# Revit family: КП РАШВОРК  арт.777 .rfa
name_source: partatom
category: Арматура трубопроводов
units: mm (PartAtom-declared; Revit-internal decimal feet)

## family parameters
Всегда вертикально = Нет
На основе рабочей плоскости = Нет
Общий = Нет
При загрузке вырезать с полостями = Да
Размер круглого соединителя = Использовать диаметр
Тип детали = Нормальный

## types (11) — shared parameters
ADSK_Единица измерения = шт
ADSK_Завод-изготовитель = ООО "ТД "РАШВОРК"
URL = https://rwru.ru
Изготовитель = ООО "ТД "РАШВОРК"
Корпус = Латунь CW617N
zero-valued in all types: Отметка по умолчанию

## per-type parameters (varying)
| type | ADSK_Код изделия | ADSK_Масса | ADSK_Наименование | L | Соединитель | Уго_длинна |
| Кран пробковый для манометра РАШВОРК 777-015-25, DN015, PN25, корпус - латунь (CW617N), конус - латунь (CW617N), уплотнение - Viton, ВР/ВР, BSPP, рукоятка-рычаг | 777-015-25 | 0.195 | Кран пробковый для манометра РАШВОРК 777-015-25, DN015, PN25, корпус - латунь (CW617N), конус - латунь (CW617N), уплотнение - Viton, ВР/ВР, BSPP, рукоятка-рычаг | 60 мм | 15 мм | 60 мм |
| Кран шаровой полнопроходной РАШВОРК 707-040-16, DN040, PN16, корпус - GJL-250 (GG25), шар - AISI304, уплотнение шара - PTFE, Ф/Ф | 707-040-16 | 7.5 | Кран шаровой полнопроходной РАШВОРК 707-040-16, DN040, PN16, корпус - GJL-250 (GG25), шар - AISI304, уплотнение шара - PTFE, Ф/Ф | 140 мм | 40 мм | 140 мм |
| Кран шаровой полнопроходной РАШВОРК 707-020-16, DN020, PN16, корпус - GJL-250 (GG25), шар - AISI304, уплотнение шара - PTFE, Ф/ | 707-020-16 | 2 | Кран шаровой полнопроходной РАШВОРК 707-020-16, DN020, PN16, корпус - GJL-250 (GG25), шар - AISI304, уплотнение шара - PTFE, Ф/Ф | 120 мм | 20 мм | 120 мм |
| Кран шаровой полнопроходной РАШВОРК 707-025-16, DN025, PN16, корпус - GJL-250 (GG25), шар - AISI304, уплотнение шара - PTFE, Ф/Ф | 707-025-16 | 2.1 | Кран шаровой полнопроходной РАШВОРК 707-025-16, DN025, PN16, корпус - GJL-250 (GG25), шар - AISI304, уплотнение шара - PTFE, Ф/Ф | 125 мм | 25 мм | 125 мм |
| Кран шаровой полнопроходной РАШВОРК 707-032-16, DN032, PN16, корпус - GJL-250 (GG25), шар - AISI304, уплотнение шара - PTFE, Ф/Ф | 707-032-16 | 5.9 | Кран шаровой полнопроходной РАШВОРК 707-032-16, DN032, PN16, корпус - GJL-250 (GG25), шар - AISI304, уплотнение шара - PTFE, Ф/Ф | 130 мм | 32 мм | 130 мм |
| Кран шаровой полнопроходной РАШВОРК 707-050-16, DN050, PN16, корпус - GJL-250 (GG25), шар - AISI304, уплотнение шара - PTFE, Ф/Ф | 707-050-16 | 8.5 | Кран шаровой полнопроходной РАШВОРК 707-050-16, DN050, PN16, корпус - GJL-250 (GG25), шар - AISI304, уплотнение шара - PTFE, Ф/Ф | 150 мм | 50 мм | 150 мм |
| Кран шаровой полнопроходной РАШВОРК 707-065-16, DN065, PN16, корпус - GJL-250 (GG25), шар - AISI304, уплотнение шара - PTFE, Ф/Ф | 707-065-16 | 13 | Кран шаровой полнопроходной РАШВОРК 707-065-16, DN065, PN16, корпус - GJL-250 (GG25), шар - AISI304, уплотнение шара - PTFE, Ф/Ф | 170 мм | 65 мм | 170 мм |
| Кран шаровой полнопроходной РАШВОРК 707-080-16, DN080, PN16, корпус - GJL-250 (GG25), шар - AISI304, уплотнение шара - PTFE, Ф/Ф | 707-080-16 | 20.5 | Кран шаровой полнопроходной РАШВОРК 707-080-16, DN080, PN16, корпус - GJL-250 (GG25), шар - AISI304, уплотнение шара - PTFE, Ф/Ф | 180 мм | 80 мм | 180 мм |
| Кран шаровой полнопроходной РАШВОРК 707-100-16, DN100, PN16, корпус - GJL-250 (GG25), шар - AISI304, уплотнение шара - PTFE, Ф/Ф | 707-100-16 | 28 | Кран шаровой полнопроходной РАШВОРК 707-100-16, DN100, PN16, корпус - GJL-250 (GG25), шар - AISI304, уплотнение шара - PTFE, Ф/Ф | 190 мм | 100 мм | 190 мм |
| Кран шаровой полнопроходной РАШВОРК 707-125-16, DN125, PN16, корпус - GJL-250 (GG25), шар - AISI304, уплотнение шара - PTFE, Ф/Ф | 707-125-16 | 49.5 | Кран шаровой полнопроходной РАШВОРК 707-125-16, DN125, PN16, корпус - GJL-250 (GG25), шар - AISI304, уплотнение шара - PTFE, Ф/Ф | 325 мм | 125 мм | 325 мм |
| Кран шаровой полнопроходной РАШВОРК 707-150-16, DN150, PN16, корпус - GJL-250 (GG25), шар - AISI304, уплотнение шара - PTFE, Ф/Ф | 707-150-16 | 67.5 | Кран шаровой полнопроходной РАШВОРК 707-150-16, DN150, PN16, корпус - GJL-250 (GG25), шар - AISI304, уплотнение шара - PTFE, Ф/Ф | 350 мм | 150 мм | 350 мм |
